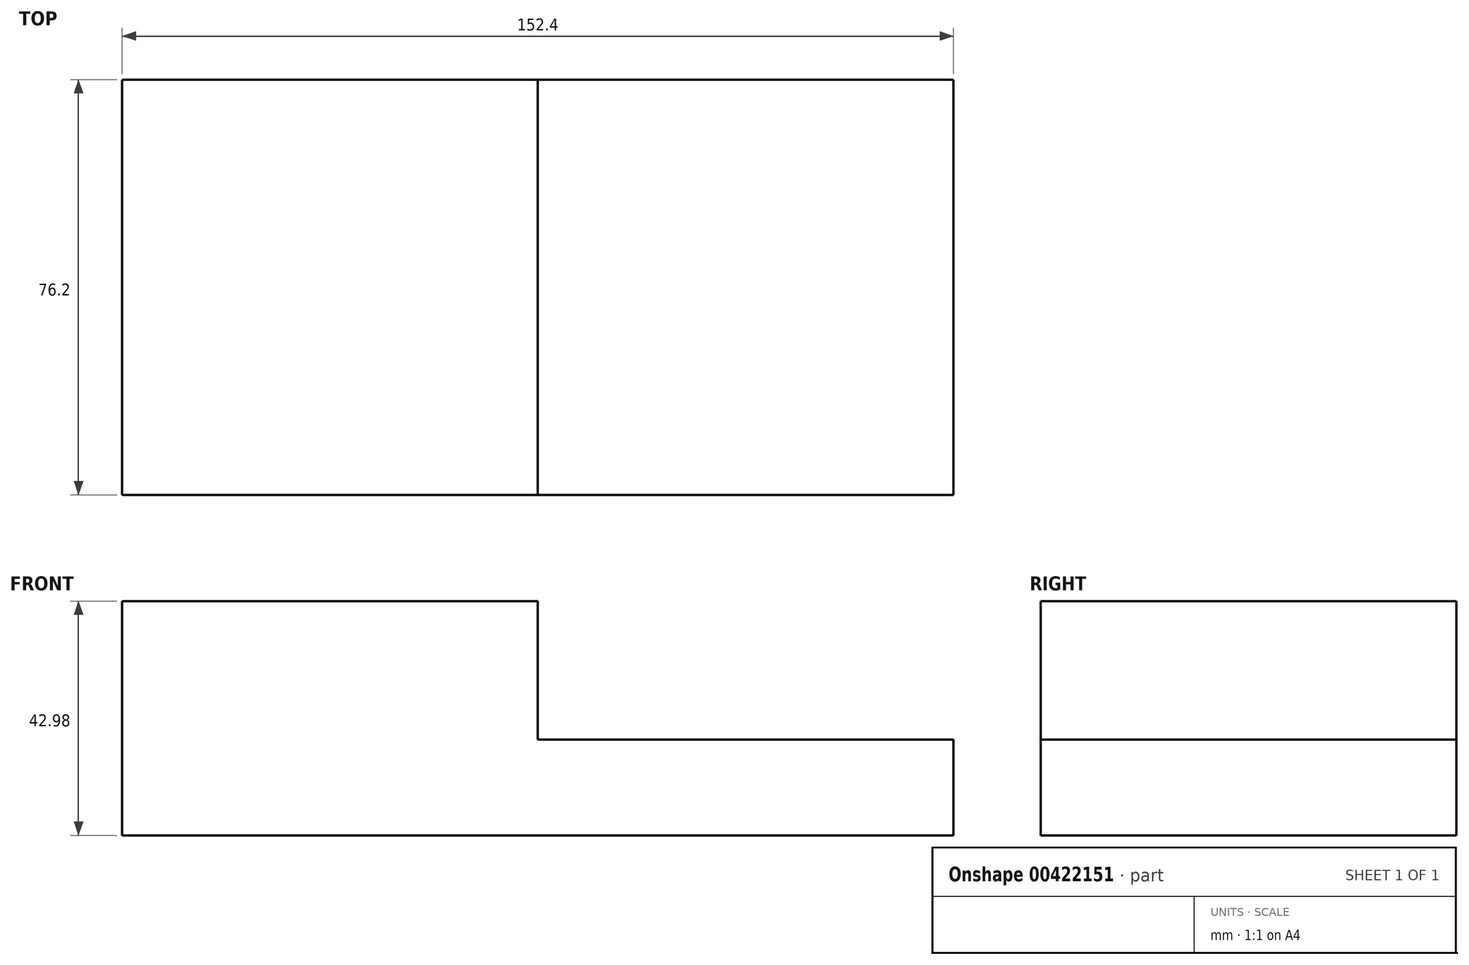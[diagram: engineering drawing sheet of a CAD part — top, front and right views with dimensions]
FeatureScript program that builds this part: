
annotation { "Feature Type Name" : "Feature", "Feature Type Description" : "" }
export const myFeature = defineFeature(function(context is Context, id is Id, definition is map)
    precondition{}
    {
        {
            var Q0;
            Q0=qCreatedBy(makeId("Front.planeOp"),FACE);
            var sketch = newSketch(context, id + "F0", { "sketchPlane" : qUnion([Q0])});
            skLineSegment(sketch, "E0", {"start": v(0, 0) * mm, "end": v(152.4, 0) * mm});
            skLineSegment(sketch, "E1", {"start": v(152.4, 0) * mm, "end": v(152.4, 17.58) * mm});
            skLineSegment(sketch, "E2", {"start": v(152.4, 17.58) * mm, "end": v(76.2, 17.58) * mm});
            skLineSegment(sketch, "E3", {"start": v(76.2, 17.58) * mm, "end": v(76.2, 42.98) * mm});
            skLineSegment(sketch, "E4", {"start": v(76.2, 42.98) * mm, "end": v(0, 42.98) * mm});
            skLineSegment(sketch, "E5", {"start": v(0, 42.98) * mm, "end": v(0, 0) * mm});
            skSolve(sketch);
        }
        {
            var Q0;
            Q0=makeQuery(id+"F0.imprint","IMPRINT",FACE,{"disambiguationData":[TD([[makeQuery(id+"F0.imprint","IMPRINT",EDGE,{"derivedFrom":sQuery(id+"F0.wireOp",EDGE,"E0")}),1.0]])]});
            extrude(context, id + "F1", {"entities" : qUnion([Q0]), "depth" : 76.2 * mm});
        }
    });
